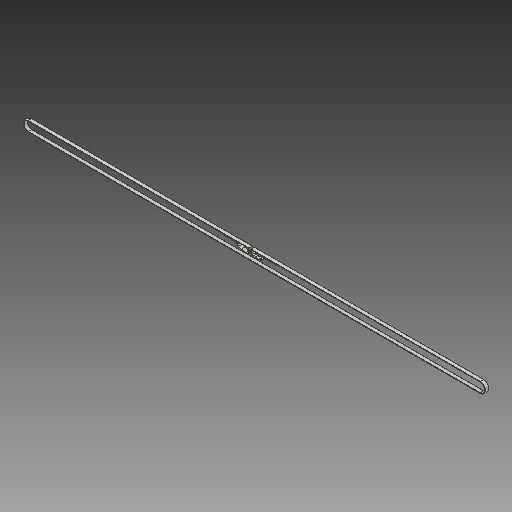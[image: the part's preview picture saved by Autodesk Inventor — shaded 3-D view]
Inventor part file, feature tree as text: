
AUTODESK INVENTOR PART (.ipt)
format: ipt  version: 2018 (Build 220112000, 112)  size: 188,416 bytes
history: native  units: mm
features: other x3, sketch x1
ambient origin geometry x8: Origin, YZ Plane, XZ Plane, XY Plane, X Axis, Y Axis, Z Axis, Center Point
bodies: Solid1 (feature_tree)
feature tree (4):
  other  "YBELT.ipt"
  other  "Solid1::YBELT.ipt"
  other  "TaggingFeature1"
  sketch  "Sketch1"  dims[d0=10.0mm]
